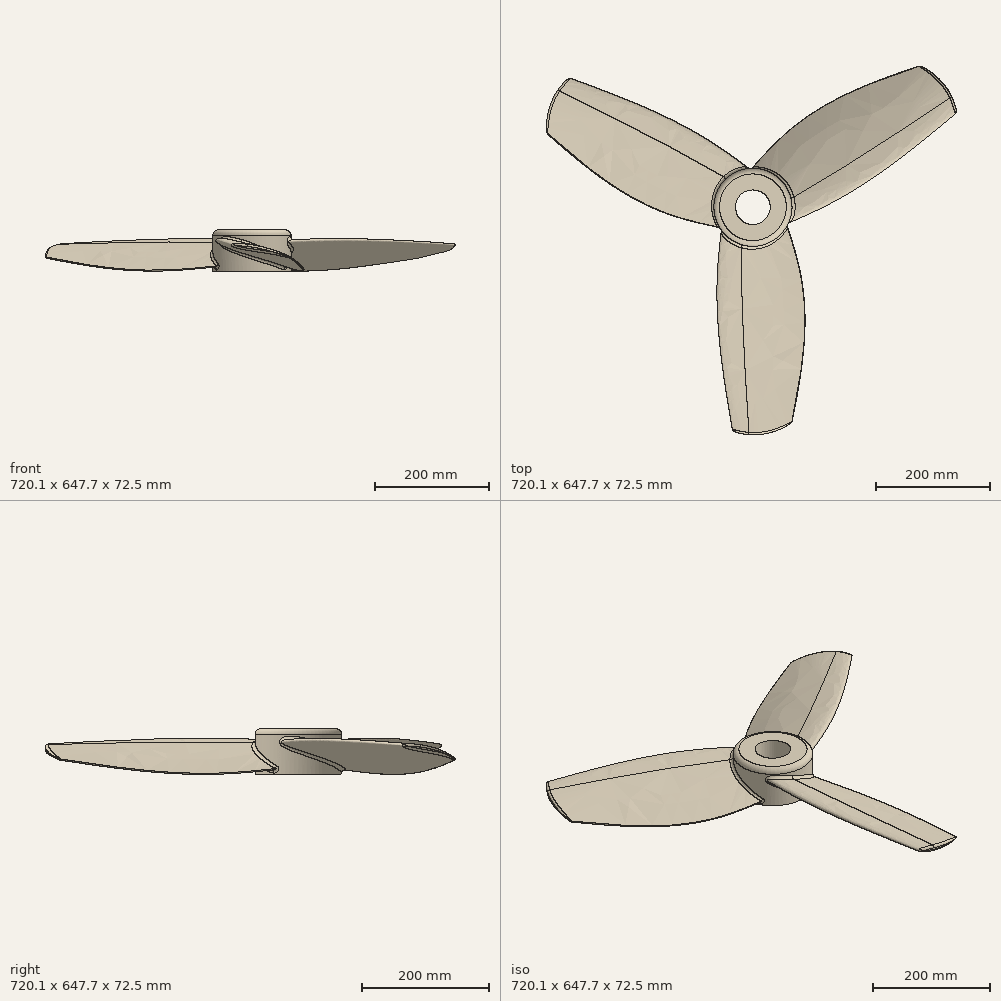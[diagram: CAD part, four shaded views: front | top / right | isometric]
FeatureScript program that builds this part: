
annotation { "Feature Type Name" : "Feature", "Feature Type Description" : "" }
export const myFeature = defineFeature(function(context is Context, id is Id, definition is map)
    precondition{}
    {
        {
            var Q0;
            Q0=qCreatedBy(makeId("Front.planeOp"),FACE);
            var sketch = newSketch(context, id + "F0", { "sketchPlane" : qUnion([Q0])});
            skLineSegment(sketch, "E0", {"start": v(-25.68, 10.16) * mm, "end": v(0, 0) * mm, "construction": true});
            skLineSegment(sketch, "E1", {"start": v(0, 0) * mm, "end": v(25.68, -10.16) * mm, "construction": true});
            skLineSegment(sketch, "E2", {"start": v(25.68, -10.16) * mm, "end": v(51.36, -20.31) * mm, "construction": true});
            skLineSegment(sketch, "E3", {"start": v(51.36, -20.31) * mm, "end": v(77.03, -30.47) * mm, "construction": true});
            skLineSegment(sketch, "E4", {"start": v(0, 0) * mm, "end": v(3.73, 9.44) * mm, "construction": true});
            skLineSegment(sketch, "E5", {"start": v(-25.68, 10.16) * mm, "end": v(-23.81, 14.88) * mm, "construction": true});
            skFitSpline(sketch, "E6", {"points": [v(-25.68, 10.16) * mm, v(3.73, 9.44) * mm, v(77.03, -30.47) * mm], "startDerivative": vector(15.03, 38) * mm, "endDerivative": vector(104.92, -93.69) * mm});
            skPoint(sketch, "E7", {"position": v(1.87, 4.72) * mm});
            skLineSegment(sketch, "E8", {"start": v(-23.81, 14.88) * mm, "end": v(1.87, 4.72) * mm, "construction": true});
            skLineSegment(sketch, "E9", {"start": v(0, 0) * mm, "end": v(-1.87, -4.72) * mm, "construction": true});
            skLineSegment(sketch, "E10", {"start": v(-25.68, 10.16) * mm, "end": v(-27.54, 5.44) * mm, "construction": true});
            skFitSpline(sketch, "E11", {"points": [v(-25.68, 10.16) * mm, v(-1.87, -4.72) * mm, v(77.03, -30.47) * mm], "startDerivative": vector(-15.23, -38.5) * mm, "endDerivative": vector(121.84, -48.19) * mm});
            skLineSegment(sketch, "E12", {"start": v(51.36, -20.31) * mm, "end": v(55.09, -10.87) * mm, "construction": true});
            skSolve(sketch);
        }
        {
            var Q0;
            Q0=qCreatedBy(makeId("Front.planeOp"),FACE);
            cPlane(context, id + "F1", {"entities" : qUnion([Q0]), "cplaneType" : CPlaneType.OFFSET, "offset" : 125 * mm, "width" : 150 * mm, "height" : 150 * mm});
        }
        {
            var Q0;
            Q0=qCreatedBy(id+"F1.planeOp",FACE);
            var sketch = newSketch(context, id + "F2", { "sketchPlane" : qUnion([Q0])});
            skLineSegment(sketch, "E13", {"start": v(-38.33, 14.06) * mm, "end": v(0, 0) * mm, "construction": true});
            skLineSegment(sketch, "E14", {"start": v(0, 0) * mm, "end": v(38.33, -14.06) * mm, "construction": true});
            skLineSegment(sketch, "E15", {"start": v(38.33, -14.06) * mm, "end": v(76.67, -28.12) * mm, "construction": true});
            skLineSegment(sketch, "E16", {"start": v(76.67, -28.12) * mm, "end": v(115, -42.17) * mm, "construction": true});
            skLineSegment(sketch, "E17", {"start": v(0, 0) * mm, "end": v(4.06, 11.06) * mm, "construction": true});
            skLineSegment(sketch, "E18", {"start": v(-38.33, 14.06) * mm, "end": v(-36.3, 19.59) * mm, "construction": true});
            skFitSpline(sketch, "E19", {"points": [v(-38.33, 14.06) * mm, v(4.06, 11.06) * mm, v(115, -42.17) * mm], "startDerivative": vector(16.44, 44.82) * mm, "endDerivative": vector(163.27, -119.63) * mm});
            skPoint(sketch, "E20", {"position": v(2.03, 5.53) * mm});
            skLineSegment(sketch, "E21", {"start": v(-36.3, 19.59) * mm, "end": v(2.03, 5.53) * mm, "construction": true});
            skLineSegment(sketch, "E22", {"start": v(0, 0) * mm, "end": v(-2.03, -5.53) * mm, "construction": true});
            skLineSegment(sketch, "E23", {"start": v(-38.33, 14.06) * mm, "end": v(-40.36, 8.53) * mm, "construction": true});
            skFitSpline(sketch, "E24", {"points": [v(-38.33, 14.06) * mm, v(-2.03, -5.53) * mm, v(115, -42.17) * mm], "startDerivative": vector(-16.57, -45.19) * mm, "endDerivative": vector(181.7, -66.64) * mm});
            skLineSegment(sketch, "E25", {"start": v(76.67, -28.12) * mm, "end": v(80.72, -17.06) * mm, "construction": true});
            skSolve(sketch);
        }
        {
            var Q0;
            Q0=qCreatedBy(makeId("Front.planeOp"),FACE);
            cPlane(context, id + "F3", {"entities" : qUnion([Q0]), "cplaneType" : CPlaneType.OFFSET, "offset" : 400 * mm, "width" : 150 * mm, "height" : 150 * mm});
        }
        {
            var Q0;
            Q0=qCreatedBy(id+"F3.planeOp",FACE);
            var sketch = newSketch(context, id + "F4", { "sketchPlane" : qUnion([Q0])});
            skLineSegment(sketch, "E26", {"start": v(-10.03, 5.14) * mm, "end": v(16.27, 0) * mm, "construction": true});
            skLineSegment(sketch, "E27", {"start": v(16.27, 0) * mm, "end": v(42.56, -5.14) * mm, "construction": true});
            skLineSegment(sketch, "E28", {"start": v(42.56, -5.14) * mm, "end": v(68.86, -10.28) * mm, "construction": true});
            skLineSegment(sketch, "E29", {"start": v(68.86, -10.28) * mm, "end": v(95.16, -15.42) * mm, "construction": true});
            skLineSegment(sketch, "E30", {"start": v(16.27, 0) * mm, "end": v(17.61, 6.9) * mm, "construction": true});
            skLineSegment(sketch, "E31", {"start": v(-10.03, 5.14) * mm, "end": v(-9.36, 8.59) * mm, "construction": true});
            skFitSpline(sketch, "E32", {"points": [v(-10.03, 5.14) * mm, v(17.61, 6.9) * mm, v(95.16, -15.42) * mm], "startDerivative": vector(5.47, 28.01) * mm, "endDerivative": vector(118.7, -57.28) * mm});
            skPoint(sketch, "E33", {"position": v(16.94, 3.45) * mm});
            skLineSegment(sketch, "E34", {"start": v(-9.36, 8.59) * mm, "end": v(16.94, 3.45) * mm, "construction": true});
            skLineSegment(sketch, "E35", {"start": v(16.27, 0) * mm, "end": v(15.6, -3.45) * mm, "construction": true});
            skLineSegment(sketch, "E36", {"start": v(-10.03, 5.14) * mm, "end": v(-10.7, 1.7) * mm, "construction": true});
            skFitSpline(sketch, "E37", {"points": [v(-10.03, 5.14) * mm, v(15.6, -3.45) * mm, v(95.16, -15.42) * mm], "startDerivative": vector(-5.51, -28.2) * mm, "endDerivative": vector(124.61, -24.36) * mm});
            skLineSegment(sketch, "E38", {"start": v(68.86, -10.28) * mm, "end": v(70.2, -3.38) * mm, "construction": true});
            skSolve(sketch);
        }
        {
            var Q0;
            Q0=qSketchRegion(id+"F0",true);
            var Q1;
            Q1=qSketchRegion(id+"F2",true);
            var Q2;
            Q2=qSketchRegion(id+"F4",true);
            var Q3;
            Q3=sQuery(id+"F0.wireOp",VERTEX,"E6.1.internal");
            var Q4;
            Q4=sQuery(id+"F2.wireOp",VERTEX,"E19.1.internal");
            var Q5;
            Q5=sQuery(id+"F4.wireOp",VERTEX,"E30.end");
            loft(context, id + "F5", {"sheetProfilesArray" : [{ "sheetProfileEntities" : qUnion([Q0]) }, { "sheetProfileEntities" : qUnion([Q1]) }, { "sheetProfileEntities" : qUnion([Q2]) }], "matchConnections" : true, "connections" : [{ "connectionEntities" : qUnion([Q3, Q4, Q5]), "connectionEdgeQueries" : qUnion([]), "connectionEdgeParameters" : [] }]});
        }
        {
            var Q0;
            Q0=qCreatedBy(makeId("Top.planeOp"),FACE);
            var sketch = newSketch(context, id + "F6", { "sketchPlane" : qUnion([Q0])});
            skFitSpline(sketch, "E39", {"points": [v(-55.98, -360.47) * mm, v(39.38, -398.87) * mm, v(142.8, -333.19) * mm], "startDerivative": vector(111.22, -150.8) * mm, "endDerivative": vector(54.24, 145.78) * mm});
            skLineSegment(sketch, "E40", {"start": v(-55.98, -360.47) * mm, "end": v(-55.98, -458.75) * mm});
            skLineSegment(sketch, "E41", {"start": v(142.8, -333.19) * mm, "end": v(142.8, -458.75) * mm});
            skLineSegment(sketch, "E42", {"start": v(142.8, -458.75) * mm, "end": v(-55.98, -458.75) * mm});
            skSolve(sketch);
        }
        {
            var Q0;
            Q0=qSketchRegion(id+"F6",true);
            extrude(context, id + "F7", {"entities" : qUnion([Q0]), "operationType" : NewBodyOperationType.REMOVE, "oppositeDirection" : true, "depth" : 40.17 * mm, "symmetric" : true});
        }
        {
            var Q0;
            Q0=makeQuery(id+"F5.opLoft","SWEPT_EDGE",EDGE,{"disambiguationData":[OSD([sQuery(id+"F2.wireOp",EDGE,"E19"),sQuery(id+"F2.wireOp",EDGE,"E24"),sQuery(id+"F4.wireOp",EDGE,"E32"),sQuery(id+"F4.wireOp",EDGE,"E37")])]});
            fillet(context, id + "F8", {"entities" : qUnion([Q0]), "radius" : 1 * mm, "tangentPropagation" : true, "allowEdgeOverflow" : false});
        }
        {
            var Q0;
            Q0=makeQuery(id+"F7.boolean.opBoolean","COPY",FACE,{"derivedFrom":makeQuery(id+"F7.opExtrude","SWEPT_FACE",FACE,{"disambiguationData":[OSD([sQuery(id+"F6.wireOp",EDGE,"E39")])]})});
            fillet(context, id + "F9", {"entities" : qUnion([Q0]), "radius" : 4 * mm, "tangentPropagation" : true, "allowEdgeOverflow" : false});
        }
        {
            var Q0;
            Q0=qCreatedBy(makeId("Top.planeOp"),FACE);
            var sketch = newSketch(context, id + "F10", { "sketchPlane" : qUnion([Q0])});
            skCircle(sketch, "E43", {"center": v(24.35, 0) * mm, "radius": 68.6 * mm});
            skSolve(sketch);
        }
        {
            var Q0;
            Q0=qSketchRegion(id+"F10",true);
            extrude(context, id + "F11", {"entities" : qUnion([Q0]), "depth" : 32.31 * mm, "hasSecondDirection" : true, "secondDirectionOppositeDirection" : true, "secondDirectionDepth" : 40 * mm});
        }
        {
            var Q0;
            Q0=makeQuery(id+"F5.opLoft","SWEPT_BODY",BODY,{"disambiguationData":[OSD([makeQuery(id+"F0.imprint","IMPRINT",FACE,{"disambiguationData":[TD([[makeQuery(id+"F0.imprint","IMPRINT",EDGE,{"derivedFrom":sQuery(id+"F0.wireOp",EDGE,"E6")}),-1.0]])]}),sQuery(id+"F2.wireOp",EDGE,"E24"),makeQuery(id+"F4.imprint","IMPRINT",FACE,{"disambiguationData":[TD([[makeQuery(id+"F4.imprint","IMPRINT",EDGE,{"derivedFrom":sQuery(id+"F4.wireOp",EDGE,"E32")}),-1.0]])]})])]});
            var Q1;
            Q1=makeQuery(id+"F11.opExtrude","SWEPT_FACE",FACE,{"disambiguationData":[OSD([sQuery(id+"F10.wireOp",EDGE,"E43")])]});
            circularPattern(context, id + "F12", {"entities" : qUnion([Q0]), "axis" : qUnion([Q1]), "angle" : 360 * degree, "instanceCount" : 3, "equalSpace" : true});
        }
        {
            var Q0;
            Q0=makeQuery(id+"F12.opPattern","COPY",BODY,{"derivedFrom":makeQuery(id+"F5.opLoft","SWEPT_BODY",BODY,{"disambiguationData":[OSD([makeQuery(id+"F0.imprint","IMPRINT",FACE,{"disambiguationData":[TD([[makeQuery(id+"F0.imprint","IMPRINT",EDGE,{"derivedFrom":sQuery(id+"F0.wireOp",EDGE,"E6")}),-1.0]])]}),sQuery(id+"F2.wireOp",EDGE,"E24"),makeQuery(id+"F4.imprint","IMPRINT",FACE,{"disambiguationData":[TD([[makeQuery(id+"F4.imprint","IMPRINT",EDGE,{"derivedFrom":sQuery(id+"F4.wireOp",EDGE,"E32")}),-1.0]])]})])]}),"instanceName":"2"});
            var Q1;
            Q1=makeQuery(id+"F5.opLoft","SWEPT_BODY",BODY,{"disambiguationData":[OSD([makeQuery(id+"F0.imprint","IMPRINT",FACE,{"disambiguationData":[TD([[makeQuery(id+"F0.imprint","IMPRINT",EDGE,{"derivedFrom":sQuery(id+"F0.wireOp",EDGE,"E6")}),-1.0]])]}),sQuery(id+"F2.wireOp",EDGE,"E24"),makeQuery(id+"F4.imprint","IMPRINT",FACE,{"disambiguationData":[TD([[makeQuery(id+"F4.imprint","IMPRINT",EDGE,{"derivedFrom":sQuery(id+"F4.wireOp",EDGE,"E32")}),-1.0]])]})])]});
            var Q2;
            Q2=makeQuery(id+"F11.opExtrude","SWEPT_BODY",BODY,{"disambiguationData":[OSD([sQuery(id+"F10.wireOp",EDGE,"E43")])]});
            var Q3;
            Q3=makeQuery(id+"F12.opPattern","COPY",BODY,{"derivedFrom":makeQuery(id+"F5.opLoft","SWEPT_BODY",BODY,{"disambiguationData":[OSD([makeQuery(id+"F0.imprint","IMPRINT",FACE,{"disambiguationData":[TD([[makeQuery(id+"F0.imprint","IMPRINT",EDGE,{"derivedFrom":sQuery(id+"F0.wireOp",EDGE,"E6")}),-1.0]])]}),sQuery(id+"F2.wireOp",EDGE,"E24"),makeQuery(id+"F4.imprint","IMPRINT",FACE,{"disambiguationData":[TD([[makeQuery(id+"F4.imprint","IMPRINT",EDGE,{"derivedFrom":sQuery(id+"F4.wireOp",EDGE,"E32")}),-1.0]])]})])]}),"instanceName":"1"});
            var Q4;
            Q4=makeQuery(id+"F12.opPattern","COPY",BODY,{"derivedFrom":makeQuery(id+"F5.opLoft","SWEPT_BODY",BODY,{"disambiguationData":[OSD([makeQuery(id+"F0.imprint","IMPRINT",FACE,{"disambiguationData":[TD([[makeQuery(id+"F0.imprint","IMPRINT",EDGE,{"derivedFrom":sQuery(id+"F0.wireOp",EDGE,"E6")}),-1.0]])]}),sQuery(id+"F2.wireOp",EDGE,"E24"),makeQuery(id+"F4.imprint","IMPRINT",FACE,{"disambiguationData":[TD([[makeQuery(id+"F4.imprint","IMPRINT",EDGE,{"derivedFrom":sQuery(id+"F4.wireOp",EDGE,"E32")}),-1.0]])]})])]}),"instanceName":"4"});
            var Q5;
            Q5=makeQuery(id+"F12.opPattern","COPY",BODY,{"derivedFrom":makeQuery(id+"F5.opLoft","SWEPT_BODY",BODY,{"disambiguationData":[OSD([makeQuery(id+"F0.imprint","IMPRINT",FACE,{"disambiguationData":[TD([[makeQuery(id+"F0.imprint","IMPRINT",EDGE,{"derivedFrom":sQuery(id+"F0.wireOp",EDGE,"E6")}),-1.0]])]}),sQuery(id+"F2.wireOp",EDGE,"E24"),makeQuery(id+"F4.imprint","IMPRINT",FACE,{"disambiguationData":[TD([[makeQuery(id+"F4.imprint","IMPRINT",EDGE,{"derivedFrom":sQuery(id+"F4.wireOp",EDGE,"E32")}),-1.0]])]})])]}),"instanceName":"3"});
            booleanBodies(context, id + "F13", {"operationType" : BooleanOperationType.UNION, "tools" : qUnion([Q0, Q1, Q2, Q3, Q4, Q5])});
        }
        {
            var Q0;
            Q0=makeQuery(id+"F11.opExtrude","CAP_FACE",FACE,{"disambiguationData":[OSD([sQuery(id+"F10.wireOp",EDGE,"E43")])],"isStart":false});
            var sketch = newSketch(context, id + "F14", { "sketchPlane" : qUnion([Q0])});
            skCircle(sketch, "E44", {"center": v(24.35, 0) * mm, "radius": 30.45 * mm});
            skSolve(sketch);
        }
        {
            var Q0;
            Q0=qSketchRegion(id+"F14",true);
            extrude(context, id + "F15", {"entities" : qUnion([Q0]), "operationType" : NewBodyOperationType.REMOVE, "endBound" : BoundingType.THROUGH_ALL, "oppositeDirection" : true, "depth" : 25 * mm});
        }
        {
            var Q0;
            {var subQ0=sQuery(id+"F0.wireOp",VERTEX,"E6.1.internal");var subQ1=sQuery(id+"F0.wireOp",EDGE,"E6");var subQ2=sQuery(id+"F0.wireOp",EDGE,"E11");var subQ3=sQuery(id+"F2.wireOp",VERTEX,"E19.1.internal");var subQ4=sQuery(id+"F2.wireOp",EDGE,"E19");var subQ5=sQuery(id+"F2.wireOp",EDGE,"E24");Q0=makeQuery(id+"F13.opBoolean","INTERSECT",EDGE,{"derivedFrom":[makeQuery(id+"F11.opExtrude","SWEPT_FACE",FACE,{"disambiguationData":[OSD([sQuery(id+"F10.wireOp",EDGE,"E43")])]}),makeQuery(id+"F12.opPattern","COPY",FACE,{"derivedFrom":makeQuery(id+"F5.opLoft","SWEPT_FACE",FACE,{"disambiguationData":[OSD([subQ0,subQ1,subQ2,subQ3,subQ4,subQ5]),TDD([subQ0,makeQuery(id+"F0.imprint","INTERSECT",VERTEX,{"disambiguationData":[OD(0.0)],"derivedFrom":[subQ1,subQ2]}),makeQuery(id+"F0.imprint","IMPRINT",EDGE,{"derivedFrom":subQ1}),subQ3,makeQuery(id+"F2.imprint","INTERSECT",VERTEX,{"disambiguationData":[OD(0.0)],"derivedFrom":[subQ4,subQ5]}),makeQuery(id+"F2.imprint","IMPRINT",EDGE,{"derivedFrom":subQ4})])]}),"instanceName":"2"})]});}
            var Q1;
            {var subQ0=sQuery(id+"F0.wireOp",VERTEX,"E6.1.internal");var subQ1=sQuery(id+"F0.wireOp",EDGE,"E6");var subQ2=sQuery(id+"F0.wireOp",EDGE,"E11");var subQ3=sQuery(id+"F2.wireOp",VERTEX,"E19.1.internal");var subQ4=sQuery(id+"F2.wireOp",EDGE,"E19");var subQ5=sQuery(id+"F2.wireOp",EDGE,"E24");Q1=makeQuery(id+"F13.opBoolean","INTERSECT",EDGE,{"derivedFrom":[makeQuery(id+"F5.opLoft","SWEPT_FACE",FACE,{"disambiguationData":[OSD([subQ0,subQ1,subQ2,subQ3,subQ4,subQ5]),TDD([subQ0,makeQuery(id+"F0.imprint","INTERSECT",VERTEX,{"disambiguationData":[OD(1.0)],"derivedFrom":[subQ1,subQ2]}),makeQuery(id+"F0.imprint","IMPRINT",EDGE,{"derivedFrom":subQ1}),subQ3,makeQuery(id+"F2.imprint","INTERSECT",VERTEX,{"disambiguationData":[OD(1.0)],"derivedFrom":[subQ4,subQ5]}),makeQuery(id+"F2.imprint","IMPRINT",EDGE,{"derivedFrom":subQ4})])]}),makeQuery(id+"F11.opExtrude","SWEPT_FACE",FACE,{"disambiguationData":[OSD([sQuery(id+"F10.wireOp",EDGE,"E43")])]})]});}
            var Q2;
            {var subQ0=sQuery(id+"F0.wireOp",VERTEX,"E6.1.internal");var subQ1=sQuery(id+"F0.wireOp",EDGE,"E6");var subQ2=sQuery(id+"F0.wireOp",EDGE,"E11");var subQ3=sQuery(id+"F2.wireOp",VERTEX,"E19.1.internal");var subQ4=sQuery(id+"F2.wireOp",EDGE,"E19");var subQ5=sQuery(id+"F2.wireOp",EDGE,"E24");Q2=makeQuery(id+"F13.opBoolean","INTERSECT",EDGE,{"derivedFrom":[makeQuery(id+"F11.opExtrude","SWEPT_FACE",FACE,{"disambiguationData":[OSD([sQuery(id+"F10.wireOp",EDGE,"E43")])]}),makeQuery(id+"F12.opPattern","COPY",FACE,{"derivedFrom":makeQuery(id+"F5.opLoft","SWEPT_FACE",FACE,{"disambiguationData":[OSD([subQ0,subQ1,subQ2,subQ3,subQ4,subQ5]),TDD([subQ0,makeQuery(id+"F0.imprint","INTERSECT",VERTEX,{"disambiguationData":[OD(1.0)],"derivedFrom":[subQ1,subQ2]}),makeQuery(id+"F0.imprint","IMPRINT",EDGE,{"derivedFrom":subQ1}),subQ3,makeQuery(id+"F2.imprint","INTERSECT",VERTEX,{"disambiguationData":[OD(1.0)],"derivedFrom":[subQ4,subQ5]}),makeQuery(id+"F2.imprint","IMPRINT",EDGE,{"derivedFrom":subQ4})])]}),"instanceName":"1"})]});}
            var Q3;
            {var subQ0=sQuery(id+"F0.wireOp",VERTEX,"E6.1.internal");var subQ1=sQuery(id+"F0.wireOp",EDGE,"E6");var subQ2=sQuery(id+"F0.wireOp",EDGE,"E11");var subQ3=sQuery(id+"F2.wireOp",VERTEX,"E19.1.internal");var subQ4=sQuery(id+"F2.wireOp",EDGE,"E19");var subQ5=sQuery(id+"F2.wireOp",EDGE,"E24");Q3=makeQuery(id+"F13.opBoolean","INTERSECT",EDGE,{"derivedFrom":[makeQuery(id+"F11.opExtrude","SWEPT_FACE",FACE,{"disambiguationData":[OSD([sQuery(id+"F10.wireOp",EDGE,"E43")])]}),makeQuery(id+"F12.opPattern","COPY",FACE,{"derivedFrom":makeQuery(id+"F5.opLoft","SWEPT_FACE",FACE,{"disambiguationData":[OSD([subQ0,subQ1,subQ2,subQ3,subQ4,subQ5]),TDD([subQ0,makeQuery(id+"F0.imprint","INTERSECT",VERTEX,{"disambiguationData":[OD(1.0)],"derivedFrom":[subQ1,subQ2]}),makeQuery(id+"F0.imprint","IMPRINT",EDGE,{"derivedFrom":subQ1}),subQ3,makeQuery(id+"F2.imprint","INTERSECT",VERTEX,{"disambiguationData":[OD(1.0)],"derivedFrom":[subQ4,subQ5]}),makeQuery(id+"F2.imprint","IMPRINT",EDGE,{"derivedFrom":subQ4})])]}),"instanceName":"4"})]});}
            var Q4;
            {var subQ0=sQuery(id+"F0.wireOp",VERTEX,"E6.1.internal");var subQ1=sQuery(id+"F0.wireOp",EDGE,"E6");var subQ2=sQuery(id+"F0.wireOp",EDGE,"E11");var subQ3=sQuery(id+"F2.wireOp",VERTEX,"E19.1.internal");var subQ4=sQuery(id+"F2.wireOp",EDGE,"E19");var subQ5=sQuery(id+"F2.wireOp",EDGE,"E24");Q4=makeQuery(id+"F13.opBoolean","INTERSECT",EDGE,{"derivedFrom":[makeQuery(id+"F11.opExtrude","SWEPT_FACE",FACE,{"disambiguationData":[OSD([sQuery(id+"F10.wireOp",EDGE,"E43")])]}),makeQuery(id+"F12.opPattern","COPY",FACE,{"derivedFrom":makeQuery(id+"F5.opLoft","SWEPT_FACE",FACE,{"disambiguationData":[OSD([subQ0,subQ1,subQ2,subQ3,subQ4,subQ5]),TDD([subQ0,makeQuery(id+"F0.imprint","INTERSECT",VERTEX,{"disambiguationData":[OD(0.0)],"derivedFrom":[subQ1,subQ2]}),makeQuery(id+"F0.imprint","IMPRINT",EDGE,{"derivedFrom":subQ1}),subQ3,makeQuery(id+"F2.imprint","INTERSECT",VERTEX,{"disambiguationData":[OD(0.0)],"derivedFrom":[subQ4,subQ5]}),makeQuery(id+"F2.imprint","IMPRINT",EDGE,{"derivedFrom":subQ4})])]}),"instanceName":"3"})]});}
            fillet(context, id + "F16", {"entities" : qUnion([Q0, Q1, Q2, Q3, Q4]), "radius" : 5 * mm, "tangentPropagation" : true, "allowEdgeOverflow" : false});
        }
        {
            var Q0;
            Q0=makeQuery(id+"F11.opExtrude","CAP_EDGE",EDGE,{"disambiguationData":[OSD([sQuery(id+"F10.wireOp",EDGE,"E43")])],"isStart":false});
            fillet(context, id + "F17", {"entities" : qUnion([Q0]), "radius" : 10 * mm, "tangentPropagation" : true, "allowEdgeOverflow" : false});
        }
    });
